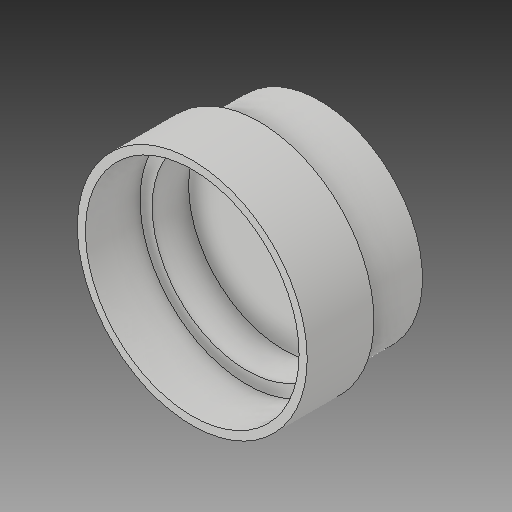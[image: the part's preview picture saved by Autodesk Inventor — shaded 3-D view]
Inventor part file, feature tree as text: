
AUTODESK INVENTOR PART (.ipt)
format: ipt  version: 2017 SP1 (Build 210196100, 196)  size: 157,184 bytes
history: native  units: mm
features: extrude x5, sketch x5
ambient origin geometry x8: Origin, YZ Plane, XZ Plane, XY Plane, X Axis, Y Axis, Z Axis, Center Point
bodies: Solid1 (feature_tree)
feature tree (10):
  extrude  "Extrusion1"  Depth=15.0mm TaperAngle=0.0deg
  extrude  "Extrusion2"  Depth=16.5mm TaperAngle=0.0deg
  extrude  "Extrusion3"  Depth=13.5mm TaperAngle=0.0deg
  extrude  "Extrusion4"  Depth=9.0mm TaperAngle=0.0deg
  extrude  "Extrusion5"  Depth=9.0mm TaperAngle=0.0deg
  sketch  "Sketch1"  dims[d0=50.8mm d1=15.0mm d2=0.0mm]
  sketch  "Sketch2"  dims[d3=56.8mm d4=16.5mm d5=0.0mm]
  sketch  "Sketch3"  dims[d6=52.8mm d7=13.5mm d8=0.0mm]
  sketch  "Sketch4"  dims[d9=46.8mm d10=9.0mm d11=0.0mm]
  sketch  "Sketch5"  dims[d12=10.0mm d13=9.0mm d14=0.0mm]
